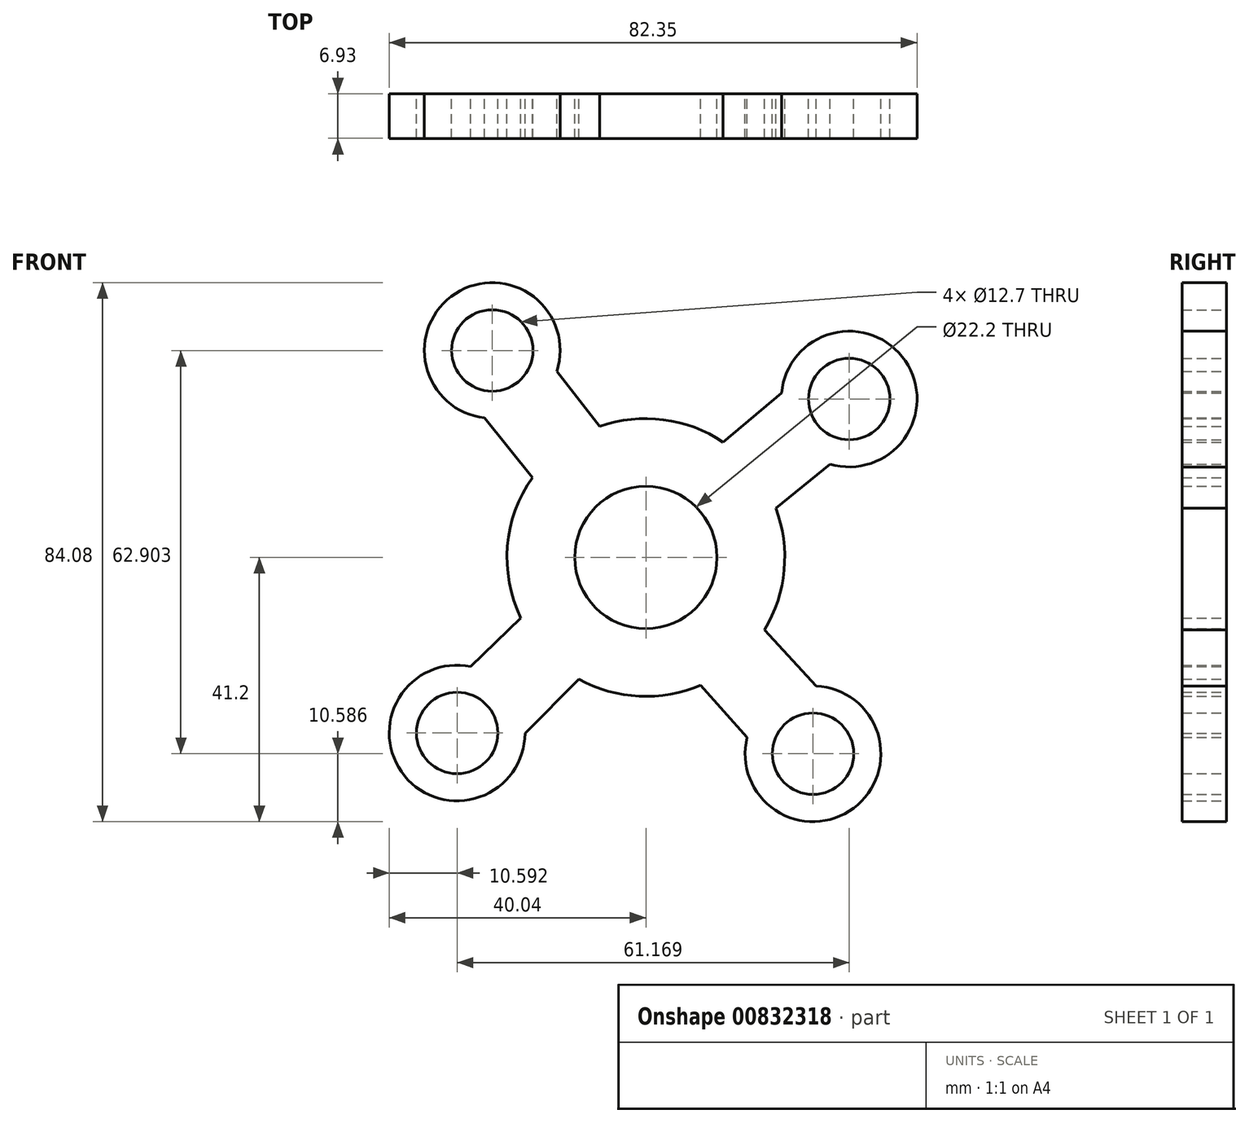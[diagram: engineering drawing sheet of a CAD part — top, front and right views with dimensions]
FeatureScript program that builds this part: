
annotation { "Feature Type Name" : "Feature", "Feature Type Description" : "" }
export const myFeature = defineFeature(function(context is Context, id is Id, definition is map)
    precondition{}
    {
        {
            var Q0;
            Q0=qCreatedBy(makeId("Front.planeOp"),FACE);
            var sketch = newSketch(context, id + "F0", { "sketchPlane" : qUnion([Q0])});
            skCircle(sketch, "E0", {"center": v(0, 0) * mm, "radius": 11.1 * mm});
            skCircle(sketch, "E1", {"center": v(-23.97, 32.29) * mm, "radius": 6.35 * mm});
            skArc(sketch, "E2", {"start": v(-13.88, 29.05) * mm, "mid": v(-29.71, 41.18) * mm, "end": v(-25.16, 21.77) * mm});
            skLineSegment(sketch, "E3", {"start": v(-25.16, 21.77) * mm, "end": v(-10.53, 3.51) * mm});
            skLineSegment(sketch, "E4", {"start": v(-13.88, 29.05) * mm, "end": v(0, 11.1) * mm});
            skLineSegment(sketch, "E5.1.0", {"start": v(28.72, 14.56) * mm, "end": v(11.1, 0.26) * mm});
            skArc(sketch, "E5.1.1", {"start": v(28.72, 14.56) * mm, "mid": v(40.48, 30.66) * mm, "end": v(21.18, 25.66) * mm});
            skCircle(sketch, "E5.1.2", {"center": v(31.72, 24.71) * mm, "radius": 6.35 * mm});
            skLineSegment(sketch, "E5.1.3", {"start": v(21.18, 25.66) * mm, "end": v(3.26, 10.6) * mm});
            skLineSegment(sketch, "E5.anchor1", {"start": v(0, 0) * mm, "end": v(0, 11.1) * mm, "construction": true});
            skLineSegment(sketch, "E5.anchor2", {"start": v(0, 0) * mm, "end": v(0.52, -11.09) * mm, "construction": true});
            skLineSegment(sketch, "E6.1.0", {"start": v(15.8, -28.06) * mm, "end": v(0.74, -11.07) * mm});
            skLineSegment(sketch, "E6.1.1", {"start": v(26.56, -20.04) * mm, "end": v(10.74, -2.8) * mm});
            skArc(sketch, "E6.1.2", {"start": v(15.8, -28.06) * mm, "mid": v(32.4, -39.1) * mm, "end": v(26.56, -20.04) * mm});
            skCircle(sketch, "E6.1.3", {"center": v(26.07, -30.61) * mm, "radius": 6.35 * mm});
            skLineSegment(sketch, "E6.2.0", {"start": v(-27.34, -17) * mm, "end": v(-11.03, -1.22) * mm});
            skLineSegment(sketch, "E6.2.1", {"start": v(-18.86, -27.4) * mm, "end": v(-2.33, -10.85) * mm});
            skArc(sketch, "E6.2.2", {"start": v(-27.34, -17) * mm, "mid": v(-37.65, -34.08) * mm, "end": v(-18.86, -27.4) * mm});
            skCircle(sketch, "E6.2.3", {"center": v(-29.45, -27.38) * mm, "radius": 6.35 * mm});
            skLineSegment(sketch, "E6.anchor1", {"start": v(0, 0) * mm, "end": v(11.1, 0.26) * mm, "construction": true});
            skLineSegment(sketch, "E6.anchor2", {"start": v(0, 0) * mm, "end": v(-11.03, -1.22) * mm, "construction": true});
            skArc(sketch, "E7", {"start": v(-17.71, 12.48) * mm, "mid": v(-21.6, 1.77) * mm, "end": v(-19.51, -9.43) * mm});
            skArc(sketch, "E8.trimOffspring", {"start": v(12.06, 18) * mm, "mid": v(2.71, 21.5) * mm, "end": v(-7.22, 20.43) * mm});
            skArc(sketch, "E9.trimOffspring", {"start": v(18.5, -11.27) * mm, "mid": v(21.58, -2) * mm, "end": v(20.26, 7.7) * mm});
            skArc(sketch, "E10.trimOffspring", {"start": v(-10.45, -18.98) * mm, "mid": v(-1.05, -21.64) * mm, "end": v(8.57, -19.9) * mm});
            skSolve(sketch);
        }
        {
            var Q0;
            {var subQ5=sQuery(id+"F0.wireOp",EDGE,"E10.trimOffspring");Q0=makeQuery(id+"F0.imprint","IMPRINT",FACE,{"disambiguationData":[TD([[makeQuery(id+"F0.imprint","IMPRINT",EDGE,{"derivedFrom":subQ5}),1.0]])]});}
            var Q1;
            {var subQ0=sQuery(id+"F0.wireOp",EDGE,"E6.1.2");Q1=makeQuery(id+"F0.imprint","IMPRINT",FACE,{"disambiguationData":[TD([[makeQuery(id+"F0.imprint","IMPRINT",EDGE,{"derivedFrom":subQ0}),1.0]])]});}
            var Q2;
            {var subQ5=sQuery(id+"F0.wireOp",EDGE,"E9.trimOffspring");Q2=makeQuery(id+"F0.imprint","IMPRINT",FACE,{"disambiguationData":[TD([[makeQuery(id+"F0.imprint","IMPRINT",EDGE,{"derivedFrom":subQ5}),1.0]])]});}
            var Q3;
            {var subQ0=sQuery(id+"F0.wireOp",EDGE,"E5.1.1");Q3=makeQuery(id+"F0.imprint","IMPRINT",FACE,{"disambiguationData":[TD([[makeQuery(id+"F0.imprint","IMPRINT",EDGE,{"derivedFrom":subQ0}),1.0]])]});}
            var Q4;
            {var subQ5=sQuery(id+"F0.wireOp",EDGE,"E8.trimOffspring");Q4=makeQuery(id+"F0.imprint","IMPRINT",FACE,{"disambiguationData":[TD([[makeQuery(id+"F0.imprint","IMPRINT",EDGE,{"derivedFrom":subQ5}),1.0]])]});}
            var Q5;
            Q5=makeQuery(id+"F0.imprint","IMPRINT",FACE,{"disambiguationData":[TD([[makeQuery(id+"F0.imprint","IMPRINT",EDGE,{"derivedFrom":sQuery(id+"F0.wireOp",EDGE,"E1")}),-1.0]])]});
            var Q6;
            {var subQ5=sQuery(id+"F0.wireOp",EDGE,"E7");Q6=makeQuery(id+"F0.imprint","IMPRINT",FACE,{"disambiguationData":[TD([[makeQuery(id+"F0.imprint","IMPRINT",EDGE,{"derivedFrom":subQ5}),1.0]])]});}
            var Q7;
            {var subQ0=sQuery(id+"F0.wireOp",EDGE,"E6.2.2");Q7=makeQuery(id+"F0.imprint","IMPRINT",FACE,{"disambiguationData":[TD([[makeQuery(id+"F0.imprint","IMPRINT",EDGE,{"derivedFrom":subQ0}),1.0]])]});}
            extrude(context, id + "F1", {"entities" : qUnion([Q0, Q1, Q2, Q3, Q4, Q5, Q6, Q7]), "depth" : 6.93 * mm, "offsetDistance" : 25.4 * mm});
        }
    });
